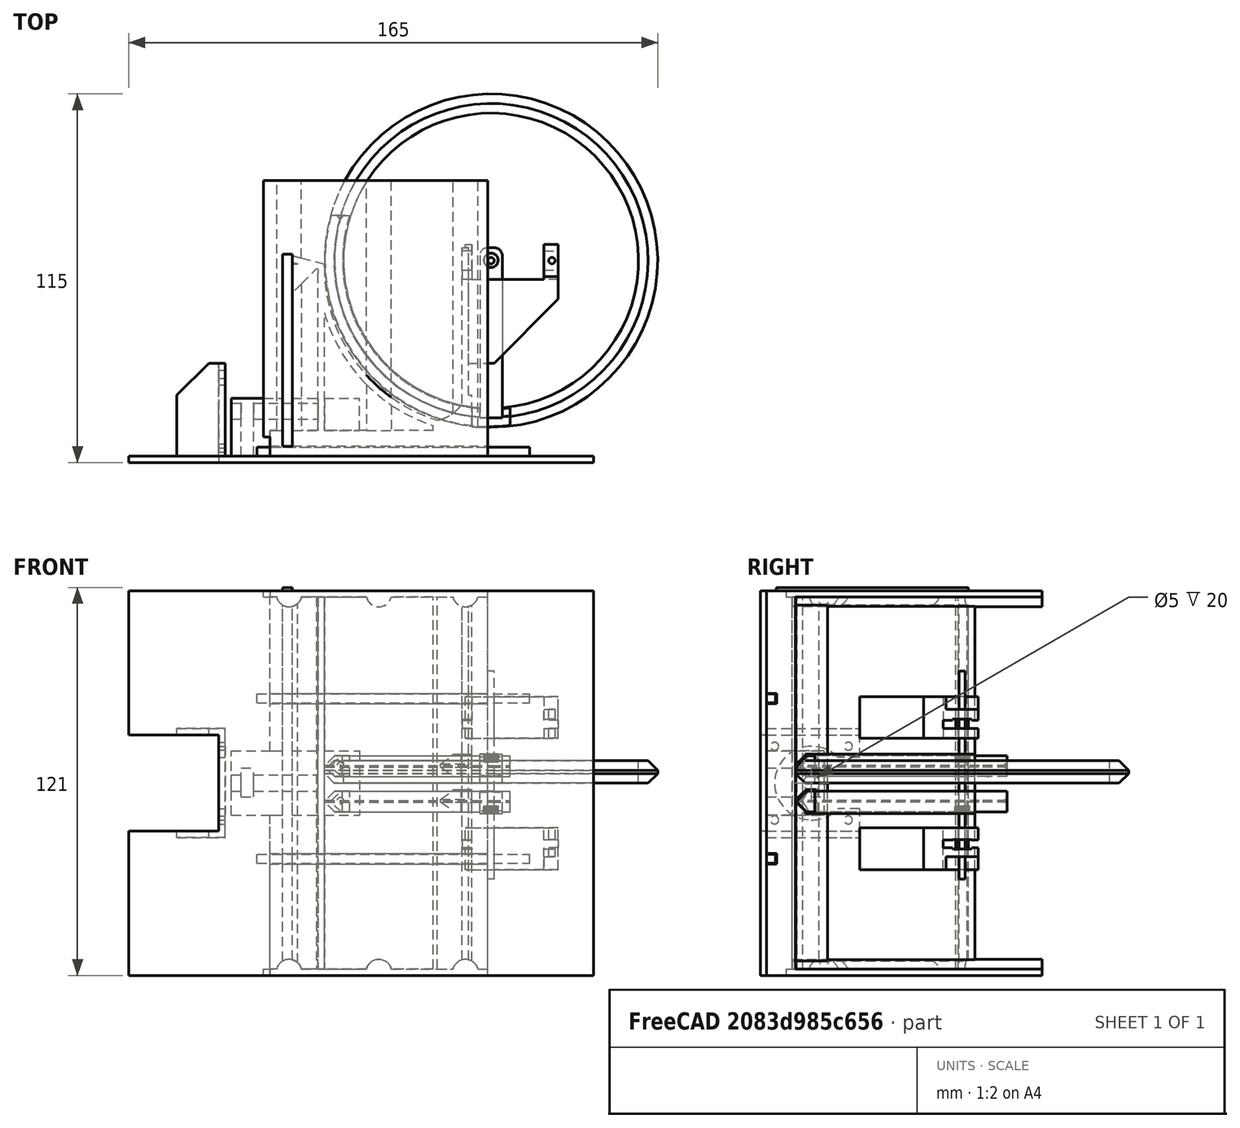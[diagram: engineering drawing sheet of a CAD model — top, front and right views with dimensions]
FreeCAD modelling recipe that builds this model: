
FCSTD DOCUMENT  (FreeCAD 0.17R13541 (Git))
Label: Hopper12_20181015
License: All rights reserved
LicenseURL: http://en.wikipedia.org/wiki/All_rights_reserved
objects: Part::Box×51, Part::Cut×50, Part::Cylinder×35, Part::MultiFuse×28, Part::Chamfer×10, Part::Cone×8, Part::MultiCommon×5, Part::Fillet×5, Part::Feature×4, Mesh::Feature×1
note: 196 computed .brp shape members not serialized (recipe doc carries the construction recipe); baked Part::Feature solids carry a one-line shape summary decoded from their .brp

FEATURE [Part::Cylinder] Cylinder003
  Angle = 360
  AttacherType = Attacher::AttachEngine3D
  Height = 120
  Placement = pos=(0,0,-60) rot=(0,0,1;0rad)
  Radius = 50
FEATURE [Part::Cylinder] Cylinder004
  Angle = 360
  AttacherType = Attacher::AttachEngine3D
  Height = 120
  Placement = pos=(0,0,-60) rot=(0,0,1;0rad)
  Radius = 52
FEATURE [Part::Cut] Cut001
  Base = -> Cylinder004
  Tool = -> Cylinder003
FEATURE [Part::Box] Box002  label="Cube002"
  AttacherType = Attacher::AttachEngine3D
  Height = 120
  Length = 70
  Placement = pos=(-69,-70,-60) rot=(0,0,1;0rad)
  Width = 70
FEATURE [Part::MultiCommon] Common001
  Placement = pos=(0,-10,0) rot=(0,0,1;0rad)
  Shapes = -> [Cut001,Box002]
FEATURE [Part::Box] Box003  label="Cube003"
  AttacherType = Attacher::AttachEngine3D
  Height = 120
  Length = 2
  Placement = pos=(-7,-54,-60) rot=(0,0,1;0rad)
  Width = 50
FEATURE [Part::MultiFuse] Fusion007002
  Shapes = -> [Common001,Box003]
FEATURE [Part::Box] Box004  label="Cube004"
  AttacherType = Attacher::AttachEngine3D
  Height = 2
  Length = 70
  Placement = pos=(-69,-63,-60) rot=(0,0,1;0rad)
  Width = 80
FEATURE [Part::Box] Box005  label="Cube005"
  AttacherType = Attacher::AttachEngine3D
  Height = 2
  Length = 70
  Placement = pos=(-69,-63,58) rot=(0,0,1;0rad)
  Width = 80
FEATURE [Part::MultiFuse] Fusion007003
  Shapes = -> [Box005,Box004,Fusion007002]
FEATURE [Part::Cylinder] Cylinder007
  Angle = 360
  AttacherType = Attacher::AttachEngine3D
  Height = 120
  Placement = pos=(-17,-46,-60) rot=(0,0,1;0rad)
  Radius = 12
FEATURE [Part::Box] Box009  label="Cube008"
  AttacherType = Attacher::AttachEngine3D
  Height = 120
  Length = 12
  Placement = pos=(-16,-63,-60) rot=(0,0,1;0rad)
  Width = 13
FEATURE [Part::Cut] Cut003
  Base = -> Box009
  Tool = -> Cylinder007
FEATURE [Part::MultiFuse] Fusion007006  label="curve"
  Placement = pos=(-2,6,0) rot=(0,0,1;0rad)
  Shapes = -> [Fusion007003,Cut003]
FEATURE [Part::Cone] Cone005
  Angle = 360
  AttacherType = Attacher::AttachEngine3D
  Height = 1
  Placement = pos=(-47,11,-4.5) rot=(-1,0,0;1.5708rad)
  Radius1 = 0.1
  Radius2 = 1
FEATURE [Part::Cylinder] Cylinder017
  Angle = 360
  AttacherType = Attacher::AttachEngine3D
  Height = 7
  Placement = pos=(2,-8,0) rot=(0,0,1;0rad)
  Radius = 52
FEATURE [Part::Cylinder] Cylinder018
  Angle = 360
  AttacherType = Attacher::AttachEngine3D
  Height = 7
  Placement = pos=(2,-8,0) rot=(0,0,1;0rad)
  Radius = 46
FEATURE [Part::Box] Box010  label="Cube009"
  AttacherType = Attacher::AttachEngine3D
  Height = 7
  Length = 53
  Placement = pos=(-4,-3.5,0) rot=(0,0,1;0rad)
  Width = 7
FEATURE [Part::Chamfer] Chamfer001
  Base = -> Cylinder017
  Edges = 2 edges r=3: [Edge1,Edge3]
FEATURE [Part::Fillet] Fillet001
  Base = -> Box010
  Edges = 2 edges r=2.4: [Edge1,Edge3]
  Placement = pos=(2,-8,0) rot=(0,0,1;0rad)
FEATURE [Part::Cut] Cut026
  Base = -> Chamfer001
  Tool = -> Cylinder018
FEATURE [Part::MultiFuse] Fusion007017
  Placement = pos=(8,0,0) rot=(0,0,-1;1.5708rad)
  Shapes = -> [Cut026,Fillet001]
FEATURE [Part::Cylinder] Cylinder019  label="pinion_donotprint001"
  Angle = 360
  AttacherType = Attacher::AttachEngine3D
  Height = 15
  Placement = pos=(0,-2,-7) rot=(0,0,1;0rad)
  Radius = 1
FEATURE [Part::Box] Box011  label="Cube010"
  AttacherType = Attacher::AttachEngine3D
  Height = 7
  Length = 53
  Placement = pos=(-4,-3.5,0) rot=(0,0,1;0rad)
  Width = 7
FEATURE [Part::Cylinder] Cylinder020
  Angle = 360
  AttacherType = Attacher::AttachEngine3D
  Height = 6.5
  Placement = pos=(2,-8,0) rot=(0,0,1;0rad)
  Radius = 51.8
FEATURE [Part::Chamfer] Chamfer002
  Base = -> Cylinder020
  Edges = 2 edges r=3: [Edge1,Edge3]
FEATURE [Part::Fillet] Fillet002
  Base = -> Box011
  Edges = 2 edges r=2.4: [Edge1,Edge3]
  Placement = pos=(2,-8,0) rot=(0,0,1;0rad)
FEATURE [Part::Cylinder] Cylinder021
  Angle = 360
  AttacherType = Attacher::AttachEngine3D
  Height = 7
  Placement = pos=(2,-8,0) rot=(0,0,1;0rad)
  Radius = 46.3
FEATURE [Part::Cut] Cut027
  Base = -> Chamfer002
  Tool = -> Cylinder021
FEATURE [Part::MultiFuse] Fusion007018
  Placement = pos=(-2,6,0) rot=(0,0,1;0rad)
  Shapes = -> [Cut027,Fillet002]
FEATURE [Part::Box] Box  label="Cube"
  AttacherType = Attacher::AttachEngine3D
  Height = 10
  Length = 66
  Placement = pos=(-14,-59,-1) rot=(0,0,1;0rad)
  Width = 63
FEATURE [Part::MultiCommon] Common  label="armL"
  Placement = pos=(0,0,1) rot=(0,0,1;0rad)
  Shapes = -> [Fusion007018,Box]
FEATURE [Part::Feature] Fusion007001  label="Servo-sg90-final_donotprint"
  Placement = pos=(16.5,-2,-36.1) rot=(0,0,1;1.5708rad)
  shape: bbox 32.4 x 11.8 x 29.9 mm, 77 faces (baked)
FEATURE [Part::Feature] Fusion007005  label="Servo-sg90-final001_donotprint"
  Placement = pos=(16.5,-2,35.5) rot=(0.707107,-0.707107,0;3.14159rad)
  shape: bbox 32.4 x 11.8 x 29.9 mm, 77 faces (baked)
FEATURE [Part::Box] Box012  label="Cube011"
  AttacherType = Attacher::AttachEngine3D
  Height = 13
  Length = 29
  Placement = pos=(-8,-13,14) rot=(0,0,1;0rad)
  Width = 16
FEATURE [Part::Box] Box013  label="Cube012"
  AttacherType = Attacher::AttachEngine3D
  Height = 13
  Length = 29
  Placement = pos=(-8,-13,-27) rot=(0,0,1;0rad)
  Width = 16
FEATURE [Part::Cylinder] Cylinder022
  Angle = 360
  AttacherType = Attacher::AttachEngine3D
  Height = 7
  Placement = pos=(2,-8,0) rot=(0,0,1;0rad)
  Radius = 46.3
FEATURE [Part::Box] Box014  label="Cube013"
  AttacherType = Attacher::AttachEngine3D
  Height = 7
  Length = 53
  Placement = pos=(-4,-3.5,-0.5) rot=(0,0,1;0rad)
  Width = 7
FEATURE [Part::Fillet] Fillet003
  Base = -> Box014
  Edges = 2 edges r=2.4: [Edge1,Edge3]
  Placement = pos=(2,-8,0) rot=(0,0,1;0rad)
FEATURE [Part::Cylinder] Cylinder023
  Angle = 360
  AttacherType = Attacher::AttachEngine3D
  Height = 6.5
  Placement = pos=(2,-8,0) rot=(0,0,1;0rad)
  Radius = 51.8
FEATURE [Part::Chamfer] Chamfer003
  Base = -> Cylinder023
  Edges = 2 edges r=3: [Edge1,Edge3]
FEATURE [Part::Cut] Cut028
  Base = -> Chamfer003
  Tool = -> Cylinder022
FEATURE [Part::MultiFuse] Fusion007019
  Placement = pos=(-2,6,0) rot=(0,0,1;0rad)
  Shapes = -> [Cut028,Fillet003]
FEATURE [Part::Box] Box015  label="Cube014"
  AttacherType = Attacher::AttachEngine3D
  Height = 10
  Length = 66
  Placement = pos=(-14,-59,-1) rot=(0,0,1;0rad)
  Width = 63
FEATURE [Part::MultiCommon] Common002  label="armR"
  Placement = pos=(0,0,-8) rot=(0,0,1;0rad)
  Shapes = -> [Fusion007019,Box015]
FEATURE [Part::MultiFuse] Fusion
  Shapes = -> [Box012,Box013]
FEATURE [Part::MultiFuse] Fusion007020  label="curve001"
  Shapes = -> [Fusion,Fusion007006]
FEATURE [Part::Cut] Cut
  Base = -> Fusion007020
  Tool = -> Fusion007005
FEATURE [Part::Cut] Cut029
  Base = -> Cut
  Tool = -> Fusion007001
FEATURE [Part::Cut] Cut030
  Base = -> Common002
  Tool = -> Fusion007001
FEATURE [Part::Cut] Cut031
  Base = -> Common
  Tool = -> Fusion007005
FEATURE [Part::Cut] Cut032  label="armL001"
  Base = -> Cut030
  Placement = pos=(2,-2,0) rot=(0,0,-1;1.5708rad)
  Tool = -> Cylinder019
FEATURE [Part::Cut] Cut033  label="armR001"
  Base = -> Cut031
  Placement = pos=(2,-2,0) rot=(0,0,-1;1.5708rad)
  Tool = -> Cylinder019
FEATURE [Part::Cylinder] Cylinder024  label="pinion_donotprint002"
  Angle = 360
  AttacherType = Attacher::AttachEngine3D
  Height = 65
  Placement = pos=(19,-2,-29) rot=(0,0,1;0rad)
  Radius = 1
FEATURE [Part::Cylinder] Cylinder025  label="pinion_donotprint003"
  Angle = 360
  AttacherType = Attacher::AttachEngine3D
  Height = 65
  Placement = pos=(22,-2,-29) rot=(0,0,1;0rad)
  Radius = 1
FEATURE [Part::Box] Box016  label="Cube015"
  AttacherType = Attacher::AttachEngine3D
  Height = 10
  Length = 10
  Placement = pos=(14,-7,23) rot=(0,0,1;0rad)
  Width = 10
FEATURE [Part::Box] Box017  label="Cube016"
  AttacherType = Attacher::AttachEngine3D
  Height = 10
  Length = 10
  Placement = pos=(14,-7,-33) rot=(0,0,1;0rad)
  Width = 10
FEATURE [Part::MultiFuse] Fusion007021
  Shapes = -> [Box017,Box016,Cylinder024,Cylinder025]
FEATURE [Part::Cut] Cut034  label="curve002"
  Base = -> Cut029
  Tool = -> Fusion007021
FEATURE [Part::Cylinder] Cylinder026  label="pinion_donotprint004"
  Angle = 360
  AttacherType = Attacher::AttachEngine3D
  Height = 65
  Placement = pos=(0,-2,-30) rot=(0,0,1;0rad)
  Radius = 1
FEATURE [Part::Cone] Cone006
  Angle = 360
  AttacherType = Attacher::AttachEngine3D
  Height = 1
  Placement = pos=(-47,11,4.5) rot=(-1,0,0;1.5708rad)
  Radius1 = 0.1
  Radius2 = 1
FEATURE [Part::Cone] Cone
  Angle = 360
  AttacherType = Attacher::AttachEngine3D
  Height = 10
  Placement = pos=(-47,12,4.5) rot=(1,0,0;1.5708rad)
  Radius1 = 1.5
  Radius2 = 5
FEATURE [Part::Cut] Cut035
  Base = -> Cut033
  Tool = -> Cone006
FEATURE [Part::Cylinder] Cylinder
  Angle = 360
  AttacherType = Attacher::AttachEngine3D
  Height = 10
  Placement = pos=(-47,2,4.5) rot=(-1,0,0;1.5708rad)
  Radius = 5
FEATURE [Part::Cut] Cut036
  Base = -> Cylinder
  Tool = -> Cone
FEATURE [Part::Cone] Cone007
  Angle = 360
  AttacherType = Attacher::AttachEngine3D
  Height = 10
  Placement = pos=(-47,12,4.5) rot=(1,0,0;1.5708rad)
  Radius1 = 1.5
  Radius2 = 5
FEATURE [Part::Cylinder] Cylinder027
  Angle = 360
  AttacherType = Attacher::AttachEngine3D
  Height = 10
  Placement = pos=(-47,2,4.5) rot=(-1,0,0;1.5708rad)
  Radius = 5
FEATURE [Part::Cut] Cut037
  Base = -> Cylinder027
  Placement = pos=(0,0,-9) rot=(0,0,1;0rad)
  Tool = -> Cone007
FEATURE [Part::Cut] Cut038  label="armL002"
  Base = -> Cut035
  Placement = pos=(0,0,1) rot=(0,0,1;0rad)
  Tool = -> Cut036
FEATURE [Part::Cut] Cut039
  Base = -> Cut032
  Tool = -> Cone005
FEATURE [Part::Cut] Cut040  label="armR002"
  Base = -> Cut039
  Placement = pos=(0,0,-1) rot=(0,0,1;0rad)
  Tool = -> Cut037
FEATURE [Part::Cylinder] Cylinder028
  Angle = 360
  AttacherType = Attacher::AttachEngine3D
  Height = 7
  Placement = pos=(2,-8,0) rot=(0,0,1;0rad)
  Radius = 46
FEATURE [Part::Cylinder] Cylinder029  label="pinion_donotprint005"
  Angle = 360
  AttacherType = Attacher::AttachEngine3D
  Height = 15
  Placement = pos=(0,-2,-7) rot=(0,0,1;0rad)
  Radius = 1
FEATURE [Part::Box] Box018  label="Cube017"
  AttacherType = Attacher::AttachEngine3D
  Height = 7
  Length = 53
  Placement = pos=(-4,-3.5,0) rot=(0,0,1;0rad)
  Width = 7
FEATURE [Part::Fillet] Fillet004
  Base = -> Box018
  Edges = 2 edges r=2.4: [Edge1,Edge3]
  Placement = pos=(2,-8,0) rot=(0,0,1;0rad)
FEATURE [Part::Cone] Cone008
  Angle = 360
  AttacherType = Attacher::AttachEngine3D
  Height = 1
  Placement = pos=(-47,11,4.5) rot=(-1,0,0;1.5708rad)
  Radius1 = 0.1
  Radius2 = 1
FEATURE [Part::Cone] Cone009
  Angle = 360
  AttacherType = Attacher::AttachEngine3D
  Height = 10
  Placement = pos=(-47,12,4.5) rot=(1,0,0;1.5708rad)
  Radius1 = 1.5
  Radius2 = 5
FEATURE [Part::Cone] Cone010
  Angle = 360
  AttacherType = Attacher::AttachEngine3D
  Height = 1
  Placement = pos=(-47,11,-4.5) rot=(-1,0,0;1.5708rad)
  Radius1 = 0.1
  Radius2 = 1
FEATURE [Part::Cylinder] Cylinder030
  Angle = 360
  AttacherType = Attacher::AttachEngine3D
  Height = 7
  Placement = pos=(2,-8,0) rot=(0,0,1;0rad)
  Radius = 52
FEATURE [Part::Chamfer] Chamfer004
  Base = -> Cylinder030
  Edges = 2 edges r=3: [Edge1,Edge3]
FEATURE [Part::Cut] Cut041
  Base = -> Chamfer004
  Tool = -> Cylinder028
FEATURE [Part::MultiFuse] Fusion007022
  Placement = pos=(-2,6,0) rot=(0,0,1;0rad)
  Shapes = -> [Cut041,Fillet004]
FEATURE [Part::Box] Box019  label="Cube018"
  AttacherType = Attacher::AttachEngine3D
  Height = 10
  Length = 66
  Placement = pos=(-14,-59,-1) rot=(0,0,1;0rad)
  Width = 63
FEATURE [Part::MultiCommon] Common003  label="armL004"
  Placement = pos=(0,0,1) rot=(0,0,1;0rad)
  Shapes = -> [Fusion007022,Box019]
FEATURE [Part::Feature] Fusion007023  label="Servo-sg90-final_donotprint001"
  Placement = pos=(16.5,-2,-36.1) rot=(0,0,1;1.5708rad)
  shape: bbox 32.4 x 11.8 x 29.9 mm, 77 faces (baked)
FEATURE [Part::Cylinder] Cylinder031
  Angle = 360
  AttacherType = Attacher::AttachEngine3D
  Height = 10
  Placement = pos=(-47,2,4.5) rot=(-1,0,0;1.5708rad)
  Radius = 5
FEATURE [Part::Feature] Fusion007024  label="Servo-sg90-final001_donotprint001"
  Placement = pos=(16.5,-2,35.9) rot=(0.707107,-0.707107,0;3.14159rad)
  shape: bbox 32.4 x 11.8 x 29.9 mm, 77 faces (baked)
FEATURE [Part::Cylinder] Cylinder032
  Angle = 360
  AttacherType = Attacher::AttachEngine3D
  Height = 7
  Placement = pos=(2,-8,0) rot=(0,0,1;0rad)
  Radius = 46
FEATURE [Part::Box] Box020  label="Cube019"
  AttacherType = Attacher::AttachEngine3D
  Height = 10
  Length = 66
  Placement = pos=(-14,-59,-1) rot=(0,0,1;0rad)
  Width = 63
FEATURE [Part::Cylinder] Cylinder033
  Angle = 360
  AttacherType = Attacher::AttachEngine3D
  Height = 7
  Placement = pos=(2,-8,0) rot=(0,0,1;0rad)
  Radius = 52
FEATURE [Part::Chamfer] Chamfer005
  Base = -> Cylinder033
  Edges = 2 edges r=3: [Edge1,Edge3]
FEATURE [Part::Cut] Cut045
  Base = -> Chamfer005
  Tool = -> Cylinder032
FEATURE [Part::Box] Box021  label="Cube020"
  AttacherType = Attacher::AttachEngine3D
  Height = 7
  Length = 53
  Placement = pos=(-4,-3.5,0) rot=(0,0,1;0rad)
  Width = 7
FEATURE [Part::Fillet] Fillet005
  Base = -> Box021
  Edges = 2 edges r=2.4: [Edge1,Edge3]
  Placement = pos=(2,-8,0) rot=(0,0,1;0rad)
FEATURE [Part::MultiFuse] Fusion007025
  Placement = pos=(-2,6,0) rot=(0,0,1;0rad)
  Shapes = -> [Cut045,Fillet005]
FEATURE [Part::MultiCommon] Common004  label="armR003"
  Placement = pos=(0,0,-8) rot=(0,0,1;0rad)
  Shapes = -> [Fusion007025,Box020]
FEATURE [Part::Cut] Cut044
  Base = -> Common004
  Tool = -> Fusion007023
FEATURE [Part::Cut] Cut042  label="armL003"
  Base = -> Cut044
  Placement = pos=(2,-2,0) rot=(0,0,-1;1.5708rad)
  Tool = -> Cylinder029
FEATURE [Part::Cone] Cone011
  Angle = 360
  AttacherType = Attacher::AttachEngine3D
  Height = 10
  Placement = pos=(-47,12,4.5) rot=(1,0,0;1.5708rad)
  Radius1 = 1.5
  Radius2 = 5
FEATURE [Part::Cut] Cut047
  Base = -> Common003
  Tool = -> Fusion007024
FEATURE [Part::Cut] Cut046  label="armR004"
  Base = -> Cut047
  Placement = pos=(2,-2,0) rot=(0,0,-1;1.5708rad)
  Tool = -> Cylinder029
FEATURE [Part::Cut] Cut048
  Base = -> Cut046
  Tool = -> Cone008
FEATURE [Part::Cut] Cut049
  Base = -> Cut042
  Tool = -> Cone010
FEATURE [Part::Cylinder] Cylinder034
  Angle = 360
  AttacherType = Attacher::AttachEngine3D
  Height = 10
  Placement = pos=(-47,2,4.5) rot=(-1,0,0;1.5708rad)
  Radius = 5
FEATURE [Part::Cut] Cut043
  Base = -> Cylinder034
  Placement = pos=(0,0,-9) rot=(0,0,1;0rad)
  Tool = -> Cone011
FEATURE [Part::Cut] Cut051  label="armR005"
  Base = -> Cut049
  Placement = pos=(0,0,-1) rot=(0,0,1;0rad)
  Tool = -> Cut043
FEATURE [Part::Cut] Cut052
  Base = -> Cylinder031
  Tool = -> Cone009
FEATURE [Part::Cut] Cut050  label="armL005"
  Base = -> Cut048
  Placement = pos=(0,0,1) rot=(0,0,1;0rad)
  Tool = -> Cut052
FEATURE [Part::MultiFuse] Fusion007026  label="Arm007026"
  Shapes = -> [Cut050,Cut051]
FEATURE [Part::Cut] Cut053  label="curve003"
  Base = -> Cut034
  Tool = -> Fusion007026
FEATURE [Part::Box] Box030  label="Cube029"
  AttacherType = Attacher::AttachEngine3D
  Height = 120
  Length = 68
  Placement = pos=(-69,-63,-60) rot=(0,0,1;0rad)
  Width = 8
FEATURE [Part::Box] Box031  label="Cube030"
  AttacherType = Attacher::AttachEngine3D
  Height = 120
  Length = 12
  Placement = pos=(-64,-2,-60) rot=(0,0,-1;0.261799rad)
  Width = 2
FEATURE [Part::Box] Box086  label="Cube071"
  AttacherType = Attacher::AttachEngine3D
  Height = 3.2
  Length = 70
  Placement = pos=(-34,-16,15) rot=(0,0,1;0rad)
  Width = 3.2
FEATURE [Part::Box] Box087  label="Cube072"
  AttacherType = Attacher::AttachEngine3D
  Height = 3.2
  Length = 70
  Placement = pos=(-34,-16,65) rot=(0,0,1;0rad)
  Width = 3.2
FEATURE [Part::MultiFuse] Fusion007027  label="rails001"
  Shapes = -> [Box086,Box087]
FEATURE [Part::Cut] Cut065
  Base = -> Box030
  Tool = -> Fusion007027
FEATURE [Part::Box] Box088  label="Cube073"
  AttacherType = Attacher::AttachEngine3D
  Height = 3.2
  Length = 80
  Placement = pos=(-34,-16,15) rot=(0,0,1;0rad)
  Width = 3.2
FEATURE [Part::Box] Box089  label="Cube074"
  AttacherType = Attacher::AttachEngine3D
  Height = 3.2
  Length = 80
  Placement = pos=(-34,-16,65) rot=(0,0,1;0rad)
  Width = 3.2
FEATURE [Part::MultiFuse] Fusion007028  label="rails002"
  Placement = pos=(-38,-47,-40.2) rot=(0,0,1;0rad)
  Shapes = -> [Box088,Box089]
FEATURE [Part::Box] Box034  label="Cube033"
  AttacherType = Attacher::AttachEngine3D
  Height = 9
  Length = 4
  Placement = pos=(3,0,5.75) rot=(0,0,1;0rad)
  Width = 20
FEATURE [Part::Cylinder] Cylinder035
  Angle = 360
  AttacherType = Attacher::AttachEngine3D
  Height = 40
  Placement = pos=(-11,14,10) rot=(0,1,0;1.5708rad)
  Radius = 2.5
FEATURE [Part::Box] Box035  label="Cube034"
  AttacherType = Attacher::AttachEngine3D
  Height = 20
  Length = 40
  Width = 18
FEATURE [Part::Cut] Cut066
  Base = -> Box035
  Tool = -> Cylinder035
FEATURE [Part::Cut] Cut067
  Base = -> Cut066
  Placement = pos=(-81,-63,-10) rot=(0,0,1;0rad)
  Tool = -> Box034
FEATURE [Part::Cut] Cut068
  Base = -> Cut065
  Tool = -> Fusion007028
FEATURE [Part::Box] Box090  label="Cube075"
  AttacherType = Attacher::AttachEngine3D
  Height = 120
  Length = 2
  Placement = pos=(-54,-56,-60) rot=(0,0,1;0rad)
  Width = 50
FEATURE [Part::Box] Box091  label="Cube076"
  AttacherType = Attacher::AttachEngine3D
  Height = 9
  Length = 4
  Placement = pos=(3,0,5.75) rot=(0,0,1;0rad)
  Width = 20
FEATURE [Part::Box] Box092  label="Cube077"
  AttacherType = Attacher::AttachEngine3D
  Height = 20
  Length = 40
  Width = 18
FEATURE [Part::Cylinder] Cylinder036
  Angle = 360
  AttacherType = Attacher::AttachEngine3D
  Height = 40
  Placement = pos=(-11,14,10) rot=(0,1,0;1.5708rad)
  Radius = 2.5
FEATURE [Part::Cut] Cut069
  Base = -> Box092
  Tool = -> Cylinder036
FEATURE [Part::Cut] Cut070
  Base = -> Cut069
  Placement = pos=(-81,-63,-10) rot=(0,0,1;0rad)
  Tool = -> Box091
FEATURE [Part::Cut] Cut071
  Base = -> Box090
  Tool = -> Cut070
FEATURE [Part::MultiFuse] Fusion007029  label="frontFusion"
  Shapes = -> [Cut068,Cut067,Cut071,Box031]
FEATURE [Part::MultiFuse] Fusion007030  label="hopper10a"
  Shapes = -> [Cut053,Fusion007029]
FEATURE [Part::Box] Box063  label="Cube052"
  AttacherType = Attacher::AttachEngine3D
  Height = 120
  Length = 115
  Placement = pos=(-44,-18,-20) rot=(0,0,1;0rad)
  Width = 2
FEATURE [Part::Cylinder] Cylinder060
  Angle = 360
  AttacherType = Attacher::AttachEngine3D
  Height = 4
  Placement = pos=(59,-12.5,32.5) rot=(0,1,0;1.5708rad)
  Radius = 1.25
FEATURE [Part::Cylinder] Cylinder061
  Angle = 360
  AttacherType = Attacher::AttachEngine3D
  Height = 4
  Placement = pos=(59,10.5,9.5) rot=(0,1,0;1.5708rad)
  Radius = 1.25
FEATURE [Part::Cylinder] Cylinder057
  Angle = 360
  AttacherType = Attacher::AttachEngine3D
  Height = 4
  Placement = pos=(59,-1,21) rot=(0,1,0;1.5708rad)
  Radius = 11.5
FEATURE [Part::Box] Box082  label="Cube067"
  AttacherType = Attacher::AttachEngine3D
  Height = 2.8
  Length = 85
  Placement = pos=(-34,-16,65) rot=(0,0,1;0rad)
  Width = 2.8
FEATURE [Part::Box] Box085  label="Cube070"
  AttacherType = Attacher::AttachEngine3D
  Height = 16
  Length = 10
  Placement = pos=(-51,6,32) rot=(0,0,1;0rad)
  Width = 7
FEATURE [Part::Cylinder] Cylinder058
  Angle = 360
  AttacherType = Attacher::AttachEngine3D
  Height = 4
  Placement = pos=(59,10.5,32.5) rot=(0,1,0;1.5708rad)
  Radius = 1.25
FEATURE [Part::Box] Box068  label="plane001"
  AttacherType = Attacher::AttachEngine3D
  Height = 120
  Length = 30
  Placement = pos=(53,-17,-41) rot=(0,0,1;0rad)
  Width = 2
FEATURE [Part::Box] Box064  label="Cube053"
  AttacherType = Attacher::AttachEngine3D
  Height = 30
  Length = 2
  Placement = pos=(60,-16,6) rot=(0,0,1;0rad)
  Width = 30
FEATURE [Part::Cut] Cut072
  Base = -> Box064
  Tool = -> Cylinder057
FEATURE [Part::Box] Box065  label="Cube054"
  AttacherType = Attacher::AttachEngine3D
  Height = 2
  Length = 15
  Placement = pos=(47,-16,4) rot=(0,0,1;0rad)
  Width = 30
FEATURE [Part::Chamfer] Chamfer007
  Base = -> Box065
  Edges = 1 edges r=15: [Edge3]
FEATURE [Part::Cylinder] Cylinder059
  Angle = 360
  AttacherType = Attacher::AttachEngine3D
  Height = 4
  Placement = pos=(59,-12.5,9.5) rot=(0,1,0;1.5708rad)
  Radius = 1.25
FEATURE [Part::Box] Box081  label="Cube066"
  AttacherType = Attacher::AttachEngine3D
  Height = 2.8
  Length = 85
  Placement = pos=(-34,-16,15) rot=(0,0,1;0rad)
  Width = 2.8
FEATURE [Part::MultiFuse] Fusion034  label="rails"
  Shapes = -> [Box081,Box082]
FEATURE [Part::Box] Box067  label="plane"
  AttacherType = Attacher::AttachEngine3D
  Height = 30
  Length = 28
  Placement = pos=(55,-17,4) rot=(0,0,1;0rad)
  Width = 2
FEATURE [Part::Cut] Cut064
  Base = -> Box068
  Placement = pos=(9,-33,21) rot=(0,0,1;3.14159rad)
  Tool = -> Box067
FEATURE [Part::Box] Box066  label="Cube055"
  AttacherType = Attacher::AttachEngine3D
  Height = 2
  Length = 15
  Placement = pos=(47,-16,4) rot=(0,0,1;0rad)
  Width = 30
FEATURE [Part::Chamfer] Chamfer006
  Base = -> Box066
  Edges = 1 edges r=15: [Edge3]
  Placement = pos=(0,0,32) rot=(0,0,1;0rad)
FEATURE [Part::MultiFuse] Fusion026
  Shapes = -> [Cylinder058,Cylinder061,Cylinder060,Cylinder059]
FEATURE [Part::Cut] Cut073
  Base = -> Cut072
  Tool = -> Fusion026
FEATURE [Part::MultiFuse] Fusion007031
  Placement = pos=(-106,-1,19) rot=(0,0,1;0rad)
  Shapes = -> [Chamfer007,Cut073,Chamfer006]
FEATURE [Part::MultiFuse] Fusion027  label="MotorMount2"
  Shapes = -> [Cut064,Box063,Fusion007031]
FEATURE [Part::MultiFuse] Fusion035  label="MotormountFusion035"
  Shapes = -> [Fusion027,Fusion034]
FEATURE [Part::Cut] Cut063  label="MotorMountCut063"
  Base = -> Fusion035
  Placement = pos=(-39,-47,-40) rot=(0,0,1;0rad)
  Tool = -> Box085
FEATURE [Part::Box] Box093  label="Cube078"
  AttacherType = Attacher::AttachEngine3D
  Height = 120
  Length = 3
  Placement = pos=(-65,-60,-59) rot=(0,0,1;0rad)
  Width = 60
FEATURE [Part::Box] Box094  label="Cube079"
  AttacherType = Attacher::AttachEngine3D
  Height = 20
  Length = 40
  Placement = pos=(-81,-63,-10) rot=(0,0,1;0rad)
  Width = 18
FEATURE [Part::Cut] Cut074
  Base = -> Box093
  Tool = -> Box094
FEATURE [Part::Box] Box096  label="Cube081"
  AttacherType = Attacher::AttachEngine3D
  Height = 13
  Length = 28
  Placement = pos=(-7,-38,14) rot=(0,0,1;0rad)
  Width = 26
FEATURE [Part::Chamfer] Chamfer
  Base = -> Box096
  Edges = 1 edges r=20: [Edge5]
  Placement = pos=(0,4,0) rot=(0,0,1;0rad)
FEATURE [Part::Box] Box097  label="Cube082"
  AttacherType = Attacher::AttachEngine3D
  Height = 13
  Length = 28
  Placement = pos=(-7,-38,14) rot=(0,0,1;0rad)
  Width = 26
FEATURE [Part::Chamfer] Chamfer008
  Base = -> Box097
  Edges = 1 edges r=20: [Edge5]
  Placement = pos=(0,4,-41) rot=(0,0,1;0rad)
FEATURE [Part::Box] Box098  label="Cube083"
  AttacherType = Attacher::AttachEngine3D
  Height = 3
  Length = 30
  Placement = pos=(-9,-5,17) rot=(0,0,1;0rad)
  Width = 6
FEATURE [Part::Box] Box099  label="Cube084"
  AttacherType = Attacher::AttachEngine3D
  Height = 3
  Length = 30
  Placement = pos=(-9,-5,-20.6) rot=(0,0,1;0rad)
  Width = 6
FEATURE [Part::MultiFuse] Fusion007032
  Shapes = -> [Box098,Box099]
FEATURE [Part::Cut] Cut075
  Base = -> Fusion007030
  Tool = -> Fusion007032
FEATURE [Part::MultiFuse] Fusion007033
  Shapes = -> [Chamfer,Chamfer008]
FEATURE [Part::MultiFuse] Fusion007034
  Shapes = -> [Cut075,Fusion007033]
FEATURE [Part::MultiFuse] Fusion007035
  Shapes = -> [Cut074,Fusion007034]
FEATURE [Part::Box] Box100  label="Cube085"
  AttacherType = Attacher::AttachEngine3D
  Height = 120
  Length = 10
  Placement = pos=(0,0,-60) rot=(0,0,1;0rad)
  Width = 10
FEATURE [Part::Chamfer] Chamfer009
  Base = -> Box100
  Edges = 1 edges r=9.9: [Edge5]
  Placement = pos=(-63,-13,0) rot=(0,0,1;0rad)
FEATURE [Part::Cylinder] Cylinder062
  Angle = 360
  AttacherType = Attacher::AttachEngine3D
  Height = 80
  Placement = pos=(0,25,0) rot=(1,0,0;1.5708rad)
  Radius = 4
FEATURE [Part::Box] Box101  label="Cube086"
  AttacherType = Attacher::AttachEngine3D
  Height = 10
  Length = 10
  Placement = pos=(-5,-55,0) rot=(0,0,1;0rad)
  Width = 80
FEATURE [Part::Cut] Cut076
  Base = -> Cylinder062
  Placement = pos=(-8,-2,59) rot=(0,0,1;0rad)
  Tool = -> Box101
FEATURE [Part::Box] Box102  label="Cube087"
  AttacherType = Attacher::AttachEngine3D
  Height = 10
  Length = 10
  Placement = pos=(-5,-55,0) rot=(0,0,1;0rad)
  Width = 80
FEATURE [Part::Cylinder] Cylinder063
  Angle = 360
  AttacherType = Attacher::AttachEngine3D
  Height = 80
  Placement = pos=(0,25,0) rot=(1,0,0;1.5708rad)
  Radius = 4
FEATURE [Part::Cut] Cut077
  Base = -> Cylinder063
  Placement = pos=(-63,-2,59) rot=(0,0,1;0rad)
  Tool = -> Box102
FEATURE [Part::Box] Box103  label="Cube088"
  AttacherType = Attacher::AttachEngine3D
  Height = 10
  Length = 10
  Placement = pos=(-5,-55,0) rot=(0,0,1;0rad)
  Width = 80
FEATURE [Part::Cylinder] Cylinder064
  Angle = 360
  AttacherType = Attacher::AttachEngine3D
  Height = 80
  Placement = pos=(0,25,0) rot=(1,0,0;1.5708rad)
  Radius = 4
FEATURE [Part::Cut] Cut078
  Base = -> Cylinder064
  Placement = pos=(-35,-2,59) rot=(0,0,1;0rad)
  Tool = -> Box103
FEATURE [Part::MultiFuse] Fusion007036
  Shapes = -> [Cut078,Cut076,Cut077]
FEATURE [Part::Box] Box104  label="Cube089"
  AttacherType = Attacher::AttachEngine3D
  Height = 10
  Length = 10
  Placement = pos=(-5,-55,0) rot=(0,0,1;0rad)
  Width = 80
FEATURE [Part::Box] Box105  label="Cube090"
  AttacherType = Attacher::AttachEngine3D
  Height = 10
  Length = 10
  Placement = pos=(-5,-55,0) rot=(0,0,1;0rad)
  Width = 80
FEATURE [Part::Cylinder] Cylinder065
  Angle = 360
  AttacherType = Attacher::AttachEngine3D
  Height = 80
  Placement = pos=(0,25,0) rot=(1,0,0;1.5708rad)
  Radius = 4
FEATURE [Part::Cut] Cut081
  Base = -> Cylinder065
  Placement = pos=(-35,-2,59) rot=(0,0,1;0rad)
  Tool = -> Box104
FEATURE [Part::Cylinder] Cylinder066
  Angle = 360
  AttacherType = Attacher::AttachEngine3D
  Height = 80
  Placement = pos=(0,25,0) rot=(1,0,0;1.5708rad)
  Radius = 4
FEATURE [Part::Cut] Cut079
  Base = -> Cylinder066
  Placement = pos=(-8,-2,59) rot=(0,0,1;0rad)
  Tool = -> Box105
FEATURE [Part::Cylinder] Cylinder067
  Angle = 360
  AttacherType = Attacher::AttachEngine3D
  Height = 80
  Placement = pos=(0,25,0) rot=(1,0,0;1.5708rad)
  Radius = 4
FEATURE [Part::Box] Box106  label="Cube091"
  AttacherType = Attacher::AttachEngine3D
  Height = 10
  Length = 10
  Placement = pos=(-5,-55,0) rot=(0,0,1;0rad)
  Width = 80
FEATURE [Part::Cut] Cut080
  Base = -> Cylinder067
  Placement = pos=(-63,-2,59) rot=(0,0,1;0rad)
  Tool = -> Box106
FEATURE [Part::MultiFuse] Fusion007037
  Placement = pos=(0,-34,0) rot=(1,0,0;3.14159rad)
  Shapes = -> [Cut081,Cut079,Cut080]
FEATURE [Part::MultiFuse] Fusion007038  label="hopper11a"
  Shapes = -> [Fusion007035,Fusion007036,Chamfer009,Fusion007037]
FEATURE [Mesh::Feature] Mesh  label="MotorMountCut063 (Meshed)"
